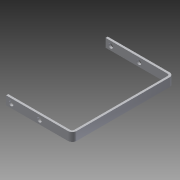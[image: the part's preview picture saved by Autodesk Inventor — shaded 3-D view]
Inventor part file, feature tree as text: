
AUTODESK INVENTOR PART (.ipt)
format: ipt  version: 2013 (Build 170138000, 138)  size: 202,752 bytes
history: native  units: in
note: dims shown in document units (in); Inventor stores cm internally (conversion verified against a paired STEP export)
features: sheet_metal_op x7, sketch x6, other x6, extrude x2, reference x2
ambient origin geometry x8: Origin, YZ Plane, XZ Plane, XY Plane, X Axis, Y Axis, Z Axis, Center Point
feature tree (23):
  sheet_metal_op  "Face2"
  sheet_metal_op  "Flange4"
  sheet_metal_op  "Flange5"
  extrude  "Extrusion3"  Depth=0.5in
  extrude  "Extrusion4"  Depth=0.125in
  sketch  "Sketch1"  dims[d1=3.619in d2=0.5in]
  other  "Plate5"
  sketch  "Sketch6"  dims[d42=0.125in]
  other  "Plate6"
  sheet_metal_op  "Bend4"
  sheet_metal_op  "Corner4"
  sketch  "Sketch7"  dims[d43=0.125in]
  other  "Plate7"
  sheet_metal_op  "Bend5"
  sheet_metal_op  "Corner5"
  sketch  "Sketch9"  dims[d44=0.0625in]
  reference  "Reference3"
  reference  "Reference4"
  sketch  "Sketch10"  dims[d45=0.25in d46=0.125in d47=5.697in d48=90.0deg d49=0.125in d50=0.5in d51=0.125in d52=0.125in d53=0.125in d54=0.0625in d55=0.25in d56=0.125in d57=3.869in d58=90.0deg d59=0.125in d60=0.5in d61=0.125in d62=0.125in d65=999.0in d66=0.0in d67=999.0in d68=0.0in d0=0.0625in d3=0.0312in d4=0.0625in d6=0.0312in d7=3.76in d9=0.0312in d10=0.0312in d11=0.0625in d12=0.125in d13=0.0in d14=0.0312in d15=0.0312in d16=0.125in d17=0.0in]
  other  "Definition1"
  sketch  "Sketch2"  dims[d5=0.295in d8=0.125in]
  other  "Cut1"
  other  "Cut2"
